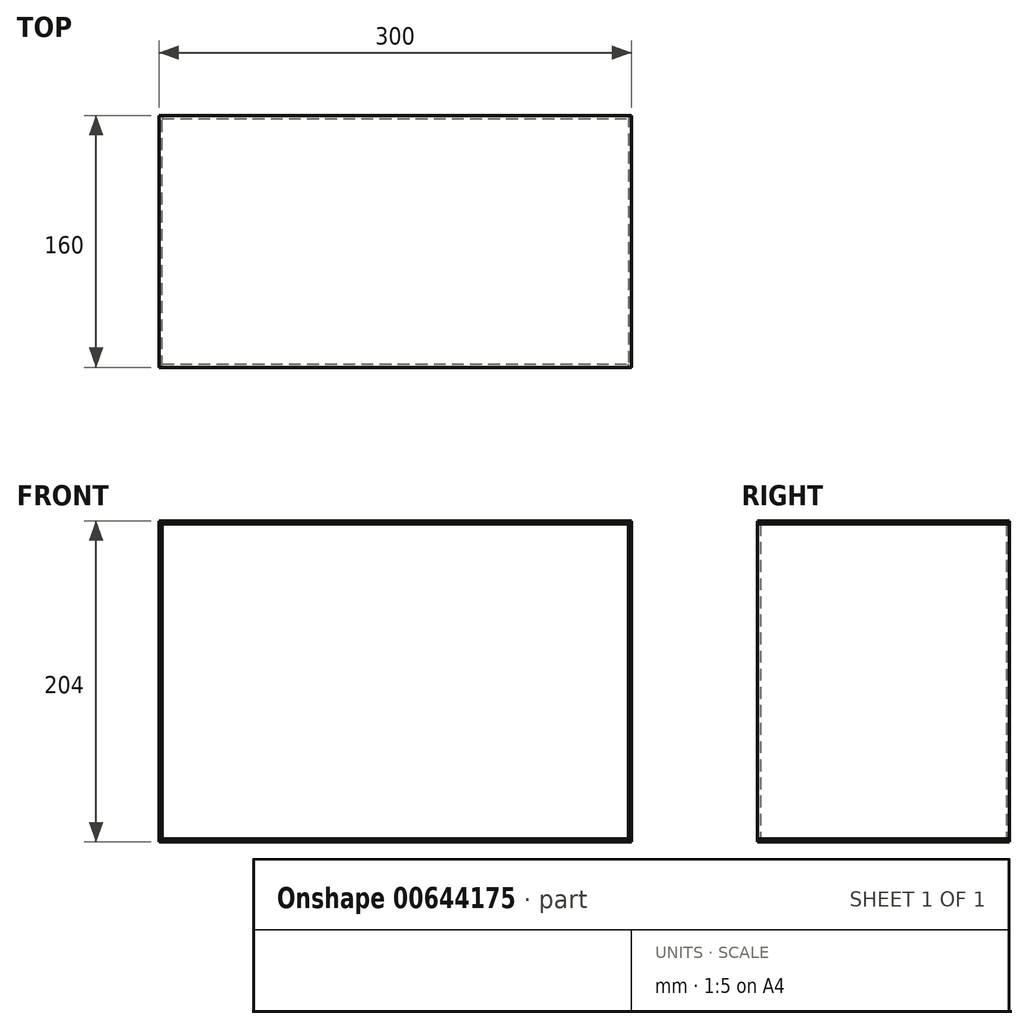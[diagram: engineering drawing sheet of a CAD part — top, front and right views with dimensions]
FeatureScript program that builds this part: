
annotation { "Feature Type Name" : "Feature", "Feature Type Description" : "" }
export const myFeature = defineFeature(function(context is Context, id is Id, definition is map)
    precondition{}
    {
        {
            var Q0;
            Q0=qCreatedBy(makeId("Top.planeOp"),FACE);
            var sketch = newSketch(context, id + "F0", { "sketchPlane" : qUnion([Q0])});
            skLineSegment(sketch, "E0.bottom", {"start": v(150, 80) * mm, "end": v(-150, 80) * mm});
            skLineSegment(sketch, "E0.top", {"start": v(150, -80) * mm, "end": v(-150, -80) * mm});
            skLineSegment(sketch, "E0.left", {"start": v(150, 80) * mm, "end": v(150, -80) * mm});
            skLineSegment(sketch, "E0.right", {"start": v(-150, 80) * mm, "end": v(-150, -80) * mm});
            skPoint(sketch, "E0.middle", {"position": v(0, 0) * mm});
            skSolve(sketch);
        }
        {
            var Q0;
            Q0 = qSketchRegion(id + "F0", true);
            extrude(context, id + "F1", {"entities" : qUnion([Q0]), "depth" : 2 * mm, "offsetDistance" : 25 * mm});
        }
        {
            var Q0;
            Q0=makeQuery(id+"F1.opExtrude","CAP_FACE",FACE,{"disambiguationData":[OSD([sQuery(id+"F0.wireOp",EDGE,"E0.bottom"),sQuery(id+"F0.wireOp",EDGE,"E0.top"),sQuery(id+"F0.wireOp",EDGE,"E0.left"),sQuery(id+"F0.wireOp",EDGE,"E0.right")])],"isStart":false});
            var sketch = newSketch(context, id + "F2", { "sketchPlane" : qUnion([Q0])});
            skLineSegment(sketch, "E1.bottom", {"start": v(-150, -80) * mm, "end": v(-148, -80) * mm});
            skLineSegment(sketch, "E1.top", {"start": v(-150, 80) * mm, "end": v(-148, 80) * mm});
            skLineSegment(sketch, "E1.left", {"start": v(-150, -80) * mm, "end": v(-150, 80) * mm});
            skLineSegment(sketch, "E1.right", {"start": v(-148, -80) * mm, "end": v(-148, 80) * mm});
            skSolve(sketch);
        }
        {
            var Q0;
            Q0 = qSketchRegion(id + "F2", true);
            extrude(context, id + "F3", {"entities" : qUnion([Q0]), "depth" : 200 * mm, "offsetDistance" : 25 * mm});
        }
        {
            var Q0;
            Q0=makeQuery(id+"F1.opExtrude","CAP_FACE",FACE,{"disambiguationData":[OSD([sQuery(id+"F0.wireOp",EDGE,"E0.bottom"),sQuery(id+"F0.wireOp",EDGE,"E0.top"),sQuery(id+"F0.wireOp",EDGE,"E0.left"),sQuery(id+"F0.wireOp",EDGE,"E0.right")])],"isStart":false});
            var sketch = newSketch(context, id + "F4", { "sketchPlane" : qUnion([Q0])});
            skLineSegment(sketch, "E2.bottom", {"start": v(150, 80) * mm, "end": v(148, 80) * mm});
            skLineSegment(sketch, "E2.top", {"start": v(150, -80) * mm, "end": v(148, -80) * mm});
            skLineSegment(sketch, "E2.left", {"start": v(150, 80) * mm, "end": v(150, -80) * mm});
            skLineSegment(sketch, "E2.right", {"start": v(148, 80) * mm, "end": v(148, -80) * mm});
            skSolve(sketch);
        }
        {
            var Q0;
            Q0 = qSketchRegion(id + "F4", true);
            extrude(context, id + "F5", {"entities" : qUnion([Q0]), "depth" : 200 * mm, "offsetDistance" : 25 * mm});
        }
        {
            var Q0;
            Q0=makeQuery(id+"F3.opExtrude","CAP_FACE",FACE,{"disambiguationData":[OSD([sQuery(id+"F2.wireOp",EDGE,"E1.bottom"),sQuery(id+"F2.wireOp",EDGE,"E1.top"),sQuery(id+"F2.wireOp",EDGE,"E1.left"),sQuery(id+"F2.wireOp",EDGE,"E1.right")])],"isStart":false});
            var sketch = newSketch(context, id + "F6", { "sketchPlane" : qUnion([Q0])});
            skLineSegment(sketch, "E3.bottom", {"start": v(-150, 80) * mm, "end": v(150, 80) * mm});
            skLineSegment(sketch, "E3.top", {"start": v(-150, -80) * mm, "end": v(150, -80) * mm});
            skLineSegment(sketch, "E3.left", {"start": v(-150, 80) * mm, "end": v(-150, -80) * mm});
            skLineSegment(sketch, "E3.right", {"start": v(150, 80) * mm, "end": v(150, -80) * mm});
            skSolve(sketch);
        }
        {
            var Q0;
            Q0 = qSketchRegion(id + "F6", true);
            extrude(context, id + "F7", {"entities" : qUnion([Q0]), "depth" : 2 * mm, "offsetDistance" : 25 * mm});
        }
        {
            var Q0;
            Q0=makeQuery(id+"F1.opExtrude","CAP_FACE",FACE,{"disambiguationData":[OSD([sQuery(id+"F0.wireOp",EDGE,"E0.bottom"),sQuery(id+"F0.wireOp",EDGE,"E0.top"),sQuery(id+"F0.wireOp",EDGE,"E0.left"),sQuery(id+"F0.wireOp",EDGE,"E0.right")])],"isStart":false});
            var sketch = newSketch(context, id + "F8", { "sketchPlane" : qUnion([Q0])});
            skLineSegment(sketch, "E4", {"start": v(-150, -80) * mm, "end": v(-148, -80) * mm});
            skLineSegment(sketch, "E5", {"start": v(150, -80) * mm, "end": v(148, -80) * mm});
            skLineSegment(sketch, "E6.bottom", {"start": v(-148, -80) * mm, "end": v(148, -80) * mm});
            skLineSegment(sketch, "E6.top", {"start": v(-148, -78) * mm, "end": v(148, -78) * mm});
            skLineSegment(sketch, "E6.left", {"start": v(-148, -80) * mm, "end": v(-148, -78) * mm});
            skLineSegment(sketch, "E6.right", {"start": v(148, -80) * mm, "end": v(148, -78) * mm});
            skSolve(sketch);
        }
        {
            var Q0;
            Q0 = qSketchRegion(id + "F8", true);
            extrude(context, id + "F9", {"entities" : qUnion([Q0]), "depth" : 200 * mm, "offsetDistance" : 25 * mm});
        }
        {
            var Q0;
            Q0=makeQuery(id+"F9.opExtrude","SWEPT_BODY",BODY,{"disambiguationData":[OSD([sQuery(id+"F8.wireOp",EDGE,"E6.bottom"),sQuery(id+"F8.wireOp",EDGE,"E6.top"),sQuery(id+"F8.wireOp",EDGE,"E6.left"),sQuery(id+"F8.wireOp",EDGE,"E6.right")])]});
            var Q1;
            Q1=qCreatedBy(makeId("Front.planeOp"),FACE);
            mirror(context, id + "F10", {"entities" : qUnion([Q0]), "mirrorPlane" : qUnion([Q1])});
        }
        {
            var Q0;
            Q0=makeQuery(id+"F3.opExtrude","CAP_FACE",FACE,{"disambiguationData":[OSD([sQuery(id+"F2.wireOp",EDGE,"E1.bottom"),sQuery(id+"F2.wireOp",EDGE,"E1.top"),sQuery(id+"F2.wireOp",EDGE,"E1.left"),sQuery(id+"F2.wireOp",EDGE,"E1.right")])],"isStart":false});
            var sketch = newSketch(context, id + "F11", { "sketchPlane" : qUnion([Q0])});
            skLineSegment(sketch, "E7.bottom", {"start": v(-150, -80) * mm, "end": v(150, -80) * mm});
            skLineSegment(sketch, "E7.top", {"start": v(-150, 80) * mm, "end": v(150, 80) * mm});
            skLineSegment(sketch, "E7.left", {"start": v(-150, -80) * mm, "end": v(-150, 80) * mm});
            skLineSegment(sketch, "E7.right", {"start": v(150, -80) * mm, "end": v(150, 80) * mm});
            skSolve(sketch);
        }
        {
            var Q0;
            Q0 = qSketchRegion(id + "F11", true);
            extrude(context, id + "F12", {"entities" : qUnion([Q0]), "depth" : 2 * mm, "offsetDistance" : 25 * mm});
        }
    });
